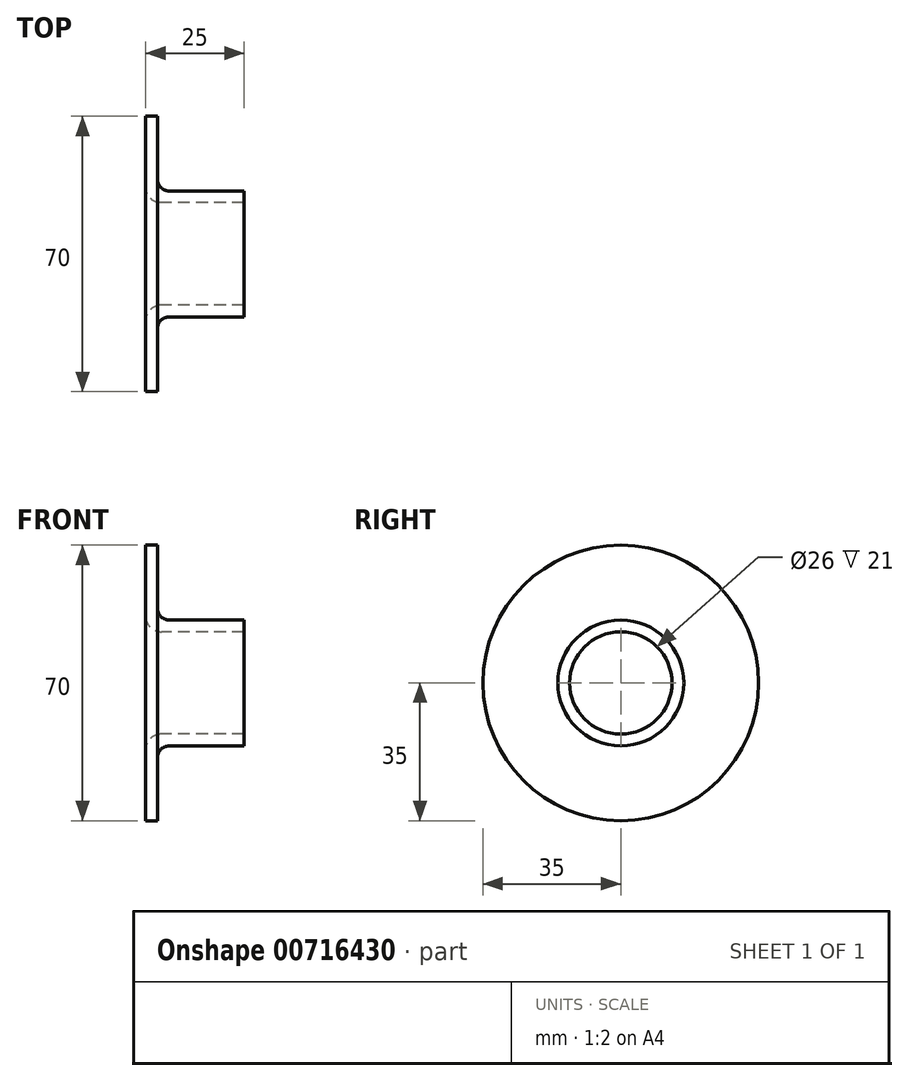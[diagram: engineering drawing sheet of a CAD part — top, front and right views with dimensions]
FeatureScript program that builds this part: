
annotation { "Feature Type Name" : "Feature", "Feature Type Description" : "" }
export const myFeature = defineFeature(function(context is Context, id is Id, definition is map)
    precondition{}
    {
        {
            var Q0;
            Q0=qCreatedBy(makeId("Top.planeOp"),FACE);
            var sketch = newSketch(context, id + "F0", { "sketchPlane" : qUnion([Q0])});
            skLineSegment(sketch, "E0", {"start": v(-43.39, 0) * mm, "end": v(69.95, 0) * mm, "construction": true});
            skLineSegment(sketch, "E1", {"start": v(0, 17) * mm, "end": v(0, 35) * mm});
            skLineSegment(sketch, "E2", {"start": v(0, 35) * mm, "end": v(3, 35) * mm});
            skLineSegment(sketch, "E3", {"start": v(3, 35) * mm, "end": v(3, 19) * mm});
            skLineSegment(sketch, "E4", {"start": v(6, 16) * mm, "end": v(25, 16) * mm});
            skLineSegment(sketch, "E5", {"start": v(25, 16) * mm, "end": v(25, 13) * mm});
            skLineSegment(sketch, "E6", {"start": v(4, 13) * mm, "end": v(25, 13) * mm});
            skPoint(sketch, "E7.visualSharp", {"position": v(0, 13) * mm});
            skArc(sketch, "E7.filletArc", {"start": v(0, 17) * mm, "mid": v(1.17, 14.17) * mm, "end": v(4, 13) * mm});
            skPoint(sketch, "E8.visualSharp", {"position": v(3, 16) * mm});
            skArc(sketch, "E8.filletArc", {"start": v(3, 19) * mm, "mid": v(3.88, 16.88) * mm, "end": v(6, 16) * mm});
            skSolve(sketch);
        }
        {
            var Q0;
            Q0 = qSketchRegion(id + "F0", true);
            var Q1;
            Q1=sQuery(id+"F0.wireOp",EDGE,"E0");
            revolve(context, id + "F1", {"surfaceOperationType" : NewSurfaceOperationType.NEW, "entities" : qUnion([Q0]), "axis" : qUnion([Q1]), "revolveType" : RevolveType.FULL});
        }
    });
